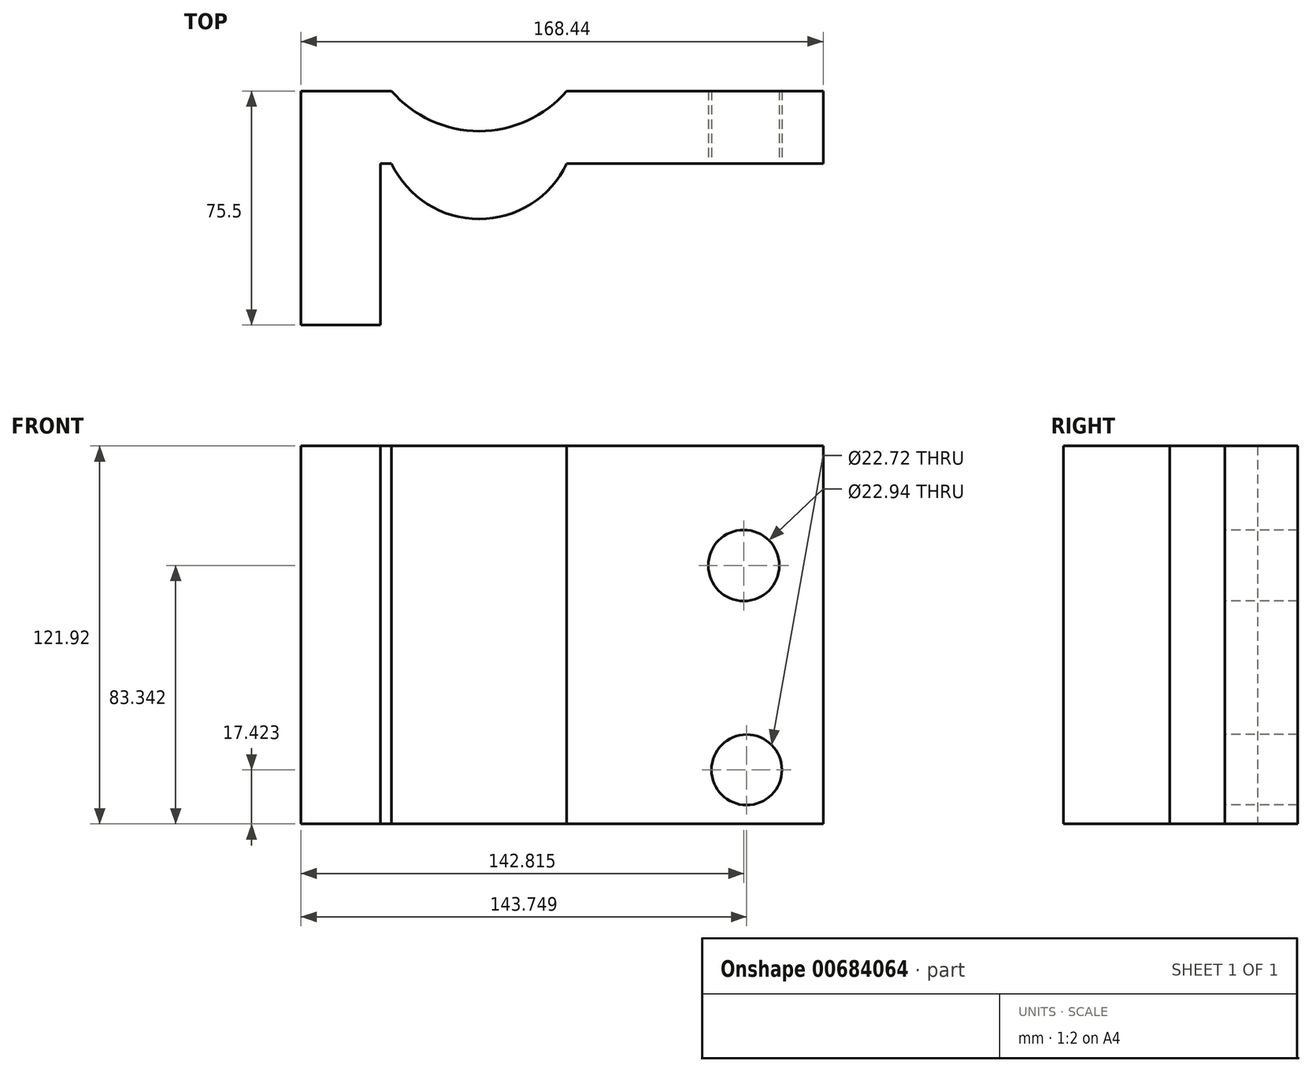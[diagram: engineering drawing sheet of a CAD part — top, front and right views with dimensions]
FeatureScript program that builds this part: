
annotation { "Feature Type Name" : "Feature", "Feature Type Description" : "" }
export const myFeature = defineFeature(function(context is Context, id is Id, definition is map)
    precondition{}
    {
        {
            var Q0;
            Q0=qCreatedBy(makeId("Top.planeOp"),FACE);
            var sketch = newSketch(context, id + "F0", { "sketchPlane" : qUnion([Q0])});
            skLineSegment(sketch, "E0", {"start": v(69.33, -7.97) * mm, "end": v(69.33, 15.5) * mm});
            skLineSegment(sketch, "E1", {"start": v(69.33, 15.5) * mm, "end": v(-13.39, 15.5) * mm});
            skLineSegment(sketch, "E2", {"start": v(-69.93, 15.5) * mm, "end": v(-99.11, 15.5) * mm});
            skLineSegment(sketch, "E3", {"start": v(-99.11, 15.5) * mm, "end": v(-99.11, -60) * mm});
            skLineSegment(sketch, "E4", {"start": v(-99.11, -60) * mm, "end": v(-73.54, -60) * mm});
            skLineSegment(sketch, "E5", {"start": v(-73.54, -60) * mm, "end": v(-73.54, -7.97) * mm});
            skLineSegment(sketch, "E6", {"start": v(-73.54, -7.97) * mm, "end": v(-69.93, -7.97) * mm});
            skLineSegment(sketch, "E7", {"start": v(69.33, -7.97) * mm, "end": v(-13.39, -7.97) * mm});
            skArc(sketch, "E8", {"start": v(-69.93, -7.97) * mm, "mid": v(-41.66, -25.83) * mm, "end": v(-13.39, -7.97) * mm});
            skArc(sketch, "E9", {"start": v(-69.93, 15.5) * mm, "mid": v(-41.66, 2.52) * mm, "end": v(-13.39, 15.5) * mm});
            skSolve(sketch);
        }
        {
            var Q0;
            Q0=makeQuery(id+"F0.imprint","IMPRINT",FACE,{"disambiguationData":[TD([[makeQuery(id+"F0.imprint","IMPRINT",EDGE,{"derivedFrom":sQuery(id+"F0.wireOp",EDGE,"E0")}),1.0]])]});
            extrude(context, id + "F1", {"entities" : qUnion([Q0]), "depth" : 121.92 * mm, "offsetDistance" : 25.4 * mm});
        }
        {
            var Q0;
            Q0=makeQuery(id+"F1.opExtrude","SWEPT_FACE",FACE,{"disambiguationData":[OSD([sQuery(id+"F0.wireOp",EDGE,"E7")])]});
            var sketch = newSketch(context, id + "F2", { "sketchPlane" : qUnion([Q0])});
            skCircle(sketch, "E10", {"center": v(44.64, 17.42) * mm, "radius": 11.36 * mm});
            skCircle(sketch, "E11", {"center": v(43.7, 83.34) * mm, "radius": 11.47 * mm});
            skSolve(sketch);
        }
        {
            var Q0;
            Q0=makeQuery(id+"F2.imprint","IMPRINT",FACE,{"disambiguationData":[TD([[makeQuery(id+"F2.imprint","IMPRINT",EDGE,{"derivedFrom":sQuery(id+"F2.wireOp",EDGE,"E11")}),1.0]])]});
            var Q1;
            Q1=makeQuery(id+"F2.imprint","IMPRINT",FACE,{"disambiguationData":[TD([[makeQuery(id+"F2.imprint","IMPRINT",EDGE,{"derivedFrom":sQuery(id+"F2.wireOp",EDGE,"E10")}),1.0]])]});
            extrude(context, id + "F3", {"entities" : qUnion([Q0, Q1]), "operationType" : NewBodyOperationType.REMOVE, "oppositeDirection" : true, "depth" : 42.67 * mm, "offsetDistance" : 25.4 * mm});
        }
    });
